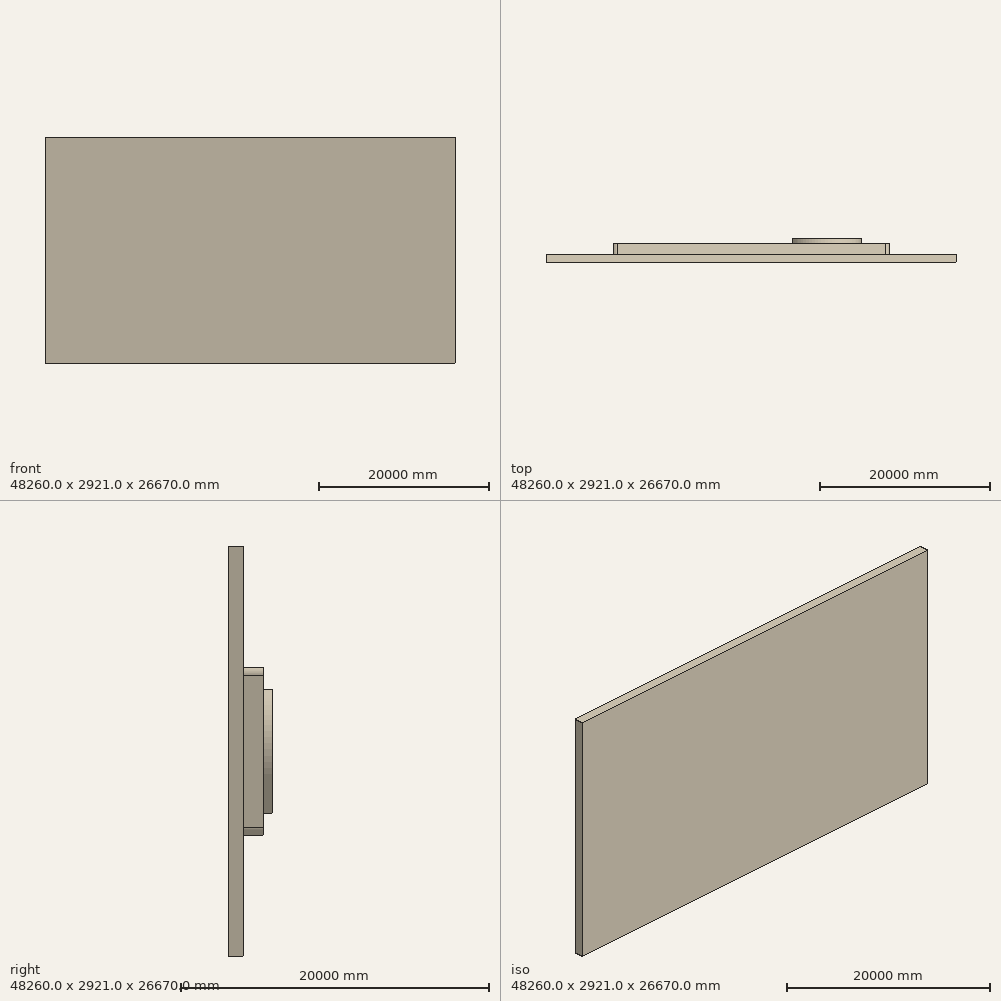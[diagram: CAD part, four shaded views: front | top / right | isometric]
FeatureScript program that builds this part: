
annotation { "Feature Type Name" : "Feature", "Feature Type Description" : "" }
export const myFeature = defineFeature(function(context is Context, id is Id, definition is map)
    precondition{}
    {
        {
            var Q0;
            Q0=qCreatedBy(makeId("Front.planeOp"),FACE);
            var sketch = newSketch(context, id + "F0", { "sketchPlane" : qUnion([Q0])});
            skLineSegment(sketch, "E0.bottom", {"start": v(24130, -13335) * mm, "end": v(-24130, -13335) * mm});
            skLineSegment(sketch, "E0.top", {"start": v(24130, 13335) * mm, "end": v(-24130, 13335) * mm});
            skLineSegment(sketch, "E0.left", {"start": v(24130, -13335) * mm, "end": v(24130, 13335) * mm});
            skLineSegment(sketch, "E0.right", {"start": v(-24130, -13335) * mm, "end": v(-24130, 13335) * mm});
            skPoint(sketch, "E0.middle", {"position": v(0, 0) * mm});
            skLineSegment(sketch, "E1.bottom", {"start": v(16256, -5461) * mm, "end": v(-16256, -5461) * mm});
            skLineSegment(sketch, "E1.top", {"start": v(16256, 5461) * mm, "end": v(-16256, 5461) * mm});
            skLineSegment(sketch, "E1.left", {"start": v(16256, -5461) * mm, "end": v(16256, 5461) * mm});
            skLineSegment(sketch, "E1.right", {"start": v(-16256, -5461) * mm, "end": v(-16256, 5461) * mm});
            skCircle(sketch, "E2", {"center": v(8890, 0) * mm, "radius": 4064 * mm});
            skLineSegment(sketch, "E3", {"start": v(0, 13335) * mm, "end": v(0, -13335) * mm, "construction": true});
            skCircle(sketch, "E4.MirrorC", {"center": v(-8890, 0) * mm, "radius": 4064 * mm, "construction": true});
            skLineSegment(sketch, "E5.0", {"start": v(15494, 4699) * mm, "end": v(-15494, 4699) * mm});
            skLineSegment(sketch, "E5.1", {"start": v(15494, -4699) * mm, "end": v(15494, 4699) * mm});
            skLineSegment(sketch, "E5.2", {"start": v(15494, -4699) * mm, "end": v(-15494, -4699) * mm});
            skLineSegment(sketch, "E5.3", {"start": v(-15494, -4699) * mm, "end": v(-15494, 4699) * mm});
            skSolve(sketch);
        }
        {
            var Q0;
            Q0 = qSketchRegion(id + "F0", true);
            var Q1;
            Q1=makeQuery(id+"F0.imprint","IMPRINT",FACE,{"disambiguationData":[TD([[makeQuery(id+"F0.imprint","IMPRINT",EDGE,{"derivedFrom":sQuery(id+"F0.wireOp",EDGE,"E2")}),-1.0]])]});
            var Q2;
            Q2=makeQuery(id+"F0.imprint","IMPRINT",FACE,{"disambiguationData":[TD([[makeQuery(id+"F0.imprint","IMPRINT",EDGE,{"derivedFrom":sQuery(id+"F0.wireOp",EDGE,"E1.bottom")}),-1.0]])]});
            var Q3;
            Q3=makeQuery(id+"F0.imprint","IMPRINT",FACE,{"disambiguationData":[TD([[makeQuery(id+"F0.imprint","IMPRINT",EDGE,{"derivedFrom":sQuery(id+"F0.wireOp",EDGE,"E2")}),1.0]])]});
            extrude(context, id + "F1", {"entities" : qUnion([Q0, Q1, Q2, Q3]), "depth" : 1016 * mm, "offsetDistance" : 25.4 * mm});
        }
        {
            var Q0;
            Q0=makeQuery(id+"F0.imprint","IMPRINT",FACE,{"disambiguationData":[TD([[makeQuery(id+"F0.imprint","IMPRINT",EDGE,{"derivedFrom":sQuery(id+"F0.wireOp",EDGE,"E1.bottom")}),-1.0]])]});
            var Q1;
            Q1=makeQuery(id+"F0.imprint","IMPRINT",FACE,{"disambiguationData":[TD([[makeQuery(id+"F0.imprint","IMPRINT",EDGE,{"derivedFrom":sQuery(id+"F0.wireOp",EDGE,"E2")}),-1.0]])]});
            extrude(context, id + "F2", {"entities" : qUnion([Q0, Q1]), "operationType" : NewBodyOperationType.ADD, "oppositeDirection" : true, "depth" : 1270 * mm, "offsetDistance" : 25.4 * mm});
        }
        {
            var Q0;
            Q0=makeQuery(id+"F0.imprint","IMPRINT",FACE,{"disambiguationData":[TD([[makeQuery(id+"F0.imprint","IMPRINT",EDGE,{"derivedFrom":sQuery(id+"F0.wireOp",EDGE,"E2")}),1.0]])]});
            extrude(context, id + "F3", {"entities" : qUnion([Q0]), "operationType" : NewBodyOperationType.ADD, "oppositeDirection" : true, "depth" : 1905 * mm, "offsetDistance" : 25.4 * mm});
        }
        {
            var Q0;
            Q0=makeQuery(id+"F2.opExtrude","SWEPT_EDGE",EDGE,{"disambiguationData":[OSD([sQuery(id+"F0.wireOp",EDGE,"E1.bottom"),sQuery(id+"F0.wireOp",EDGE,"E1.left")])]});
            var Q1;
            Q1=makeQuery(id+"F2.opExtrude","SWEPT_EDGE",EDGE,{"disambiguationData":[OSD([sQuery(id+"F0.wireOp",EDGE,"E1.top"),sQuery(id+"F0.wireOp",EDGE,"E1.left")])]});
            var Q2;
            Q2=makeQuery(id+"F2.opExtrude","SWEPT_EDGE",EDGE,{"disambiguationData":[OSD([sQuery(id+"F0.wireOp",EDGE,"E1.bottom"),sQuery(id+"F0.wireOp",EDGE,"E1.right")])]});
            var Q3;
            Q3=makeQuery(id+"F2.opExtrude","SWEPT_EDGE",EDGE,{"disambiguationData":[OSD([sQuery(id+"F0.wireOp",EDGE,"E1.top"),sQuery(id+"F0.wireOp",EDGE,"E1.right")])]});
            fillet(context, id + "F4", {"entities" : qUnion([Q0, Q1, Q2, Q3]), "radius" : 508 * mm, "tangentPropagation" : true, "allowEdgeOverflow" : false});
        }
        {
            var Q0;
            Q0=makeQuery(id+"F2.opExtrude","CAP_FACE",FACE,{"disambiguationData":[OSD([sQuery(id+"F0.wireOp",EDGE,"E1.bottom"),sQuery(id+"F0.wireOp",EDGE,"E1.top"),sQuery(id+"F0.wireOp",EDGE,"E1.left"),sQuery(id+"F0.wireOp",EDGE,"E1.right"),sQuery(id+"F0.wireOp",EDGE,"E2")])],"isStart":false});
            var sketch = newSketch(context, id + "F5", { "sketchPlane" : qUnion([Q0])});
            skLineSegment(sketch, "E6", {"start": v(-8890, 0) * mm, "end": v(-8890, -5461) * mm, "construction": true});
            skLineSegment(sketch, "E7", {"start": v(-16256, 0) * mm, "end": v(16256, 0) * mm, "construction": true});
            skArc(sketch, "E8.0", {"start": v(8890, -4064) * mm, "mid": v(12954, 0) * mm, "end": v(8890, 4064) * mm, "construction": true});
            skLineSegment(sketch, "E9.0", {"start": v(0, 13335) * mm, "end": v(0, -13335) * mm, "construction": true});
            skLineSegment(sketch, "E10", {"start": v(8890, 4064) * mm, "end": v(-8890, 4064) * mm, "construction": true});
            skArc(sketch, "E11.0", {"start": v(-8890, 4064) * mm, "mid": v(-12954, 0) * mm, "end": v(-8890, -4064) * mm, "construction": true});
            skLineSegment(sketch, "E12", {"start": v(-8890, -4064) * mm, "end": v(8890, -4064) * mm, "construction": true});
            skLineSegment(sketch, "E13.0", {"start": v(8890, 4572) * mm, "end": v(-8890, 4572) * mm});
            skArc(sketch, "E13.1", {"start": v(8890, -4572) * mm, "mid": v(13462, 0) * mm, "end": v(8890, 4572) * mm});
            skLineSegment(sketch, "E13.2", {"start": v(-8890, -4572) * mm, "end": v(8890, -4572) * mm});
            skArc(sketch, "E13.3", {"start": v(-8890, 4572) * mm, "mid": v(-13462, 0) * mm, "end": v(-8890, -4572) * mm});
            skLineSegment(sketch, "E14.0", {"start": v(-15494, -4699) * mm, "end": v(-15494, 4699) * mm, "construction": true});
            skLineSegment(sketch, "E15.0", {"start": v(-8890, 4699) * mm, "end": v(8890, 4699) * mm});
            skLineSegment(sketch, "E16.0", {"start": v(-8890, -4699) * mm, "end": v(8890, -4699) * mm});
            skFitSpline(sketch, "E17", {"points": [v(-15494, 0) * mm, v(-8890, -4699) * mm], "startDerivative": vector(0, -8105.15) * mm, "endDerivative": vector(8428.77, 0) * mm});
            skFitSpline(sketch, "E18.MirrorCS", {"points": [v(-15494, 0) * mm, v(-8890, 4699) * mm], "startDerivative": vector(0, 8105.15) * mm, "endDerivative": vector(8428.77, 0) * mm});
            skFitSpline(sketch, "E19.MirrorCS", {"points": [v(15494, 0) * mm, v(8890, -4699) * mm], "startDerivative": vector(0, -8105.15) * mm, "endDerivative": vector(-8428.77, 0) * mm});
            skFitSpline(sketch, "E20.MirrorCS", {"points": [v(15494, 0) * mm, v(8890, 4699) * mm], "startDerivative": vector(0, 8105.15) * mm, "endDerivative": vector(-8428.77, 0) * mm});
            skPoint(sketch, "E21.orphan", {"position": v(-15494, -4699) * mm});
            skPoint(sketch, "E22.orphan", {"position": v(15494, -4699) * mm});
            skPoint(sketch, "E23.orphan", {"position": v(15494, 4699) * mm});
            skPoint(sketch, "E24.orphan", {"position": v(-15494, 4699) * mm});
            skSolve(sketch);
        }
        {
            var Q0;
            Q0=makeQuery(id+"F5.imprint","IMPRINT",FACE,{"disambiguationData":[TD([[makeQuery(id+"F5.imprint","IMPRINT",EDGE,{"derivedFrom":sQuery(id+"F5.wireOp",EDGE,"E13.0")}),-1.0]])]});
            extrude(context, id + "F6", {"entities" : qUnion([Q0]), "operationType" : NewBodyOperationType.REMOVE, "oppositeDirection" : true, "depth" : 25 * mm, "offsetDistance" : 25.4 * mm});
        }
    });
